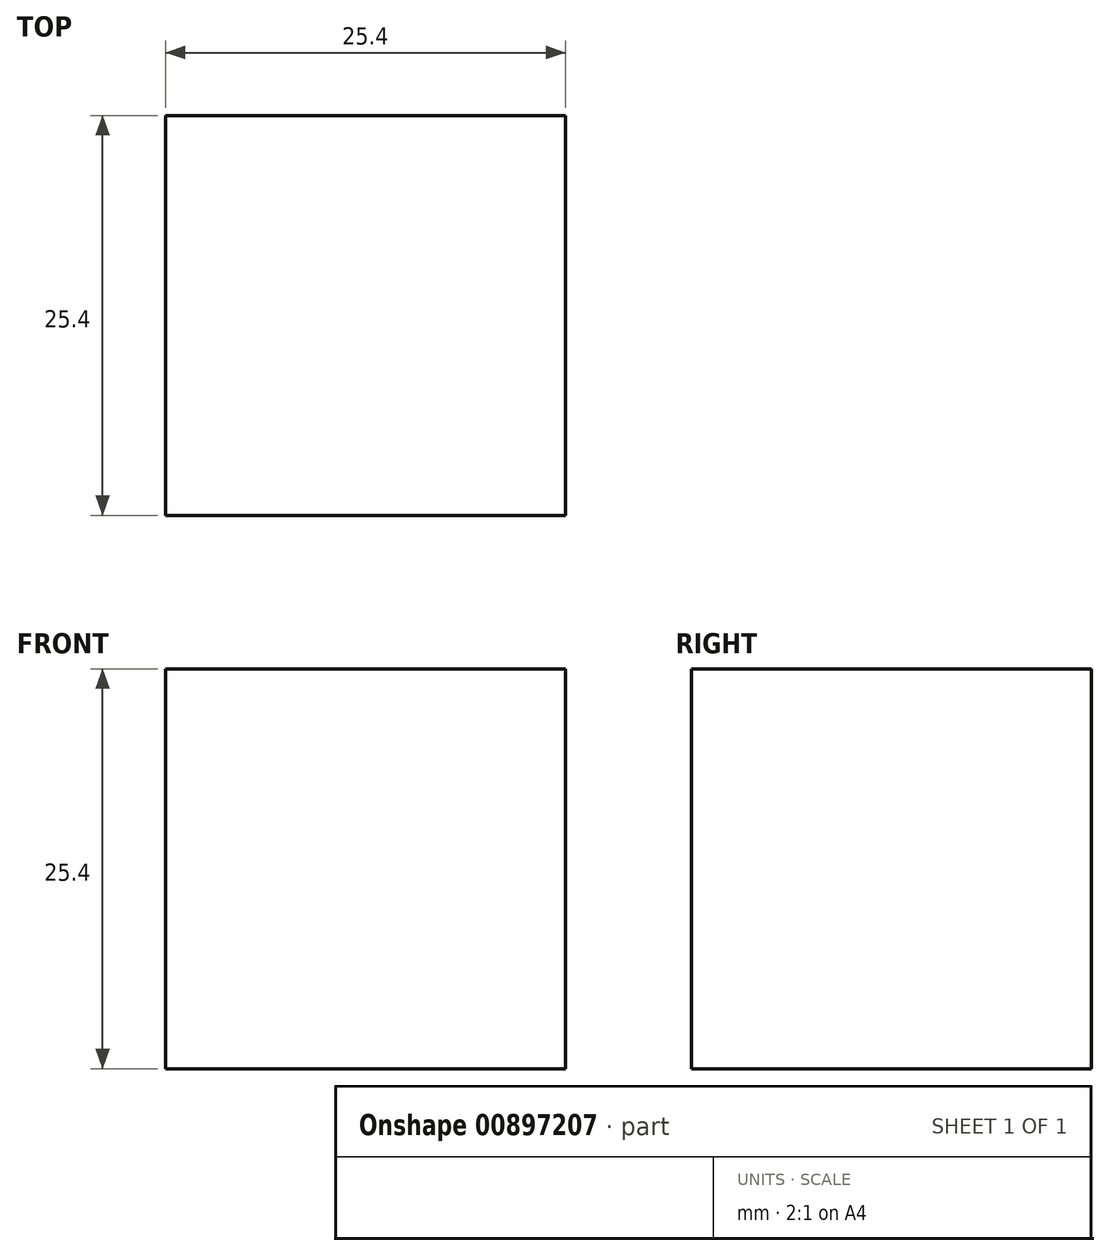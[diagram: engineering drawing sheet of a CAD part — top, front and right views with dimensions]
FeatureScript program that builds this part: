
annotation { "Feature Type Name" : "Feature", "Feature Type Description" : "" }
export const myFeature = defineFeature(function(context is Context, id is Id, definition is map)
    precondition{}
    {
        {
            var Q0;
            Q0=qCreatedBy(makeId("Front.planeOp"),FACE);
            var sketch = newSketch(context, id + "F0", { "sketchPlane" : qUnion([Q0])});
            skLineSegment(sketch, "E0.bottom", {"start": v(12.7, 12.7) * mm, "end": v(-12.7, 12.7) * mm});
            skLineSegment(sketch, "E0.top", {"start": v(12.7, -12.7) * mm, "end": v(-12.7, -12.7) * mm});
            skLineSegment(sketch, "E0.left", {"start": v(12.7, 12.7) * mm, "end": v(12.7, -12.7) * mm});
            skLineSegment(sketch, "E0.right", {"start": v(-12.7, 12.7) * mm, "end": v(-12.7, -12.7) * mm});
            skPoint(sketch, "E0.middle", {"position": v(0, 0) * mm});
            skSolve(sketch);
        }
        {
            var Q0;
            Q0 = qSketchRegion(id + "F0", true);
            extrude(context, id + "F1", {"entities" : qUnion([Q0]), "depth" : 25.4 * mm, "offsetDistance" : 25.4 * mm});
        }
    });
